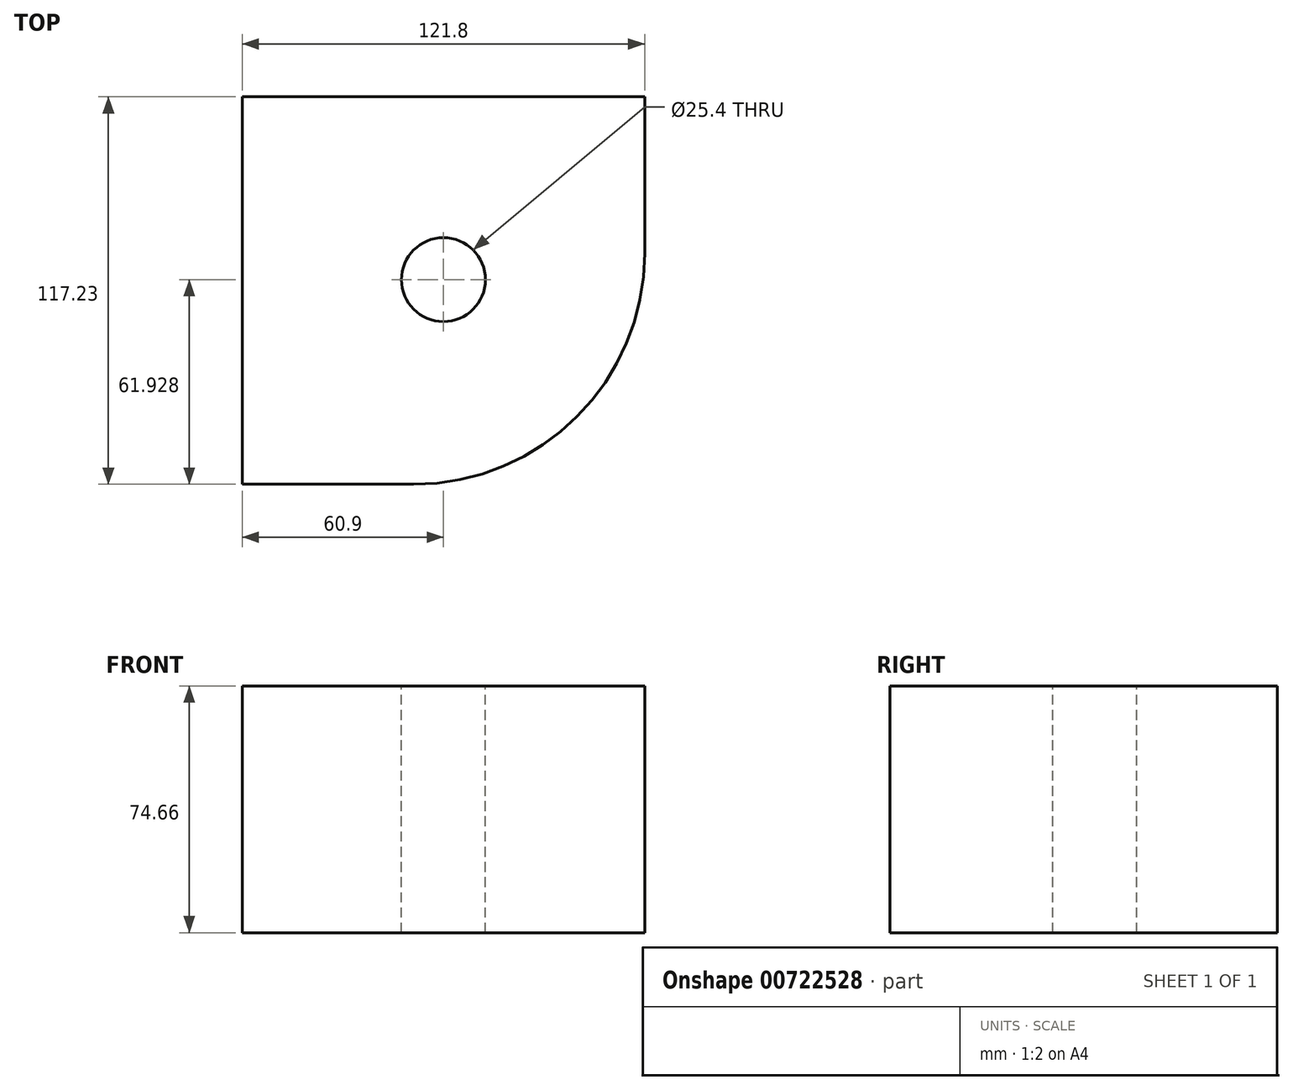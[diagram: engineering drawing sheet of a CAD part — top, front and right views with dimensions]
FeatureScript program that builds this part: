
annotation { "Feature Type Name" : "Feature", "Feature Type Description" : "" }
export const myFeature = defineFeature(function(context is Context, id is Id, definition is map)
    precondition{}
    {
        {
            var Q0;
            Q0=qCreatedBy(makeId("Front.planeOp"),FACE);
            var sketch = newSketch(context, id + "F0", { "sketchPlane" : qUnion([Q0])});
            skLineSegment(sketch, "E0.bottom", {"start": v(-60.9, 37.33) * mm, "end": v(60.9, 37.33) * mm});
            skLineSegment(sketch, "E0.top", {"start": v(-60.9, -37.33) * mm, "end": v(60.9, -37.33) * mm});
            skLineSegment(sketch, "E0.left", {"start": v(-60.9, 37.33) * mm, "end": v(-60.9, -37.33) * mm});
            skLineSegment(sketch, "E0.right", {"start": v(60.9, 37.33) * mm, "end": v(60.9, -37.33) * mm});
            skPoint(sketch, "E0.middle", {"position": v(0, 0) * mm});
            skSolve(sketch);
        }
        {
            var Q0;
            Q0=makeQuery(id+"F0.imprint","IMPRINT",FACE,{"disambiguationData":[TD([[makeQuery(id+"F0.imprint","IMPRINT",EDGE,{"derivedFrom":sQuery(id+"F0.wireOp",EDGE,"E0.bottom")}),-1.0]])]});
            extrude(context, id + "F1", {"entities" : qUnion([Q0]), "depth" : 117.23 * mm, "offsetDistance" : 25.4 * mm});
        }
        {
            var Q0;
            Q0=makeQuery(id+"F1.opExtrude","SWEPT_FACE",FACE,{"disambiguationData":[OSD([sQuery(id+"F0.wireOp",EDGE,"E0.bottom")])]});
            var sketch = newSketch(context, id + "F2", { "sketchPlane" : qUnion([Q0])});
            skCircle(sketch, "E1", {"center": v(0, -55.3) * mm, "radius": 40.23 * mm});
            skSolve(sketch);
        }
        {
            var Q0;
            Q0=sQuery(id+"F2.wireOp",VERTEX,"E1.center");
            var Q1;
            Q1=makeQuery(id+"F1.opExtrude","SWEPT_BODY",BODY,{"disambiguationData":[OSD([sQuery(id+"F0.wireOp",EDGE,"E0.bottom"),sQuery(id+"F0.wireOp",EDGE,"E0.top"),sQuery(id+"F0.wireOp",EDGE,"E0.left"),sQuery(id+"F0.wireOp",EDGE,"E0.right")])]});
            hole(context, id + "F3", {"style" : HoleStyle.SIMPLE, "endStyle" : HoleEndStyle.THROUGH, "holeDiameter" : 25.4 * mm, "majorDiameter" : 6.35 * mm, "isTappedThrough" : true, "tappedDepth" : 12.7 * mm, "tapClearance" : 3, "locations" : qUnion([Q0]), "scope" : qUnion([Q1])});
        }
        {
            var Q0;
            Q0=makeQuery(id+"F1.opExtrude","CAP_EDGE",EDGE,{"disambiguationData":[OSD([sQuery(id+"F0.wireOp",EDGE,"E0.right")])],"isStart":false});
            fillet(context, id + "F4", {"entities" : qUnion([Q0]), "radius" : 69.93 * mm, "tangentPropagation" : true, "allowEdgeOverflow" : false});
        }
    });
